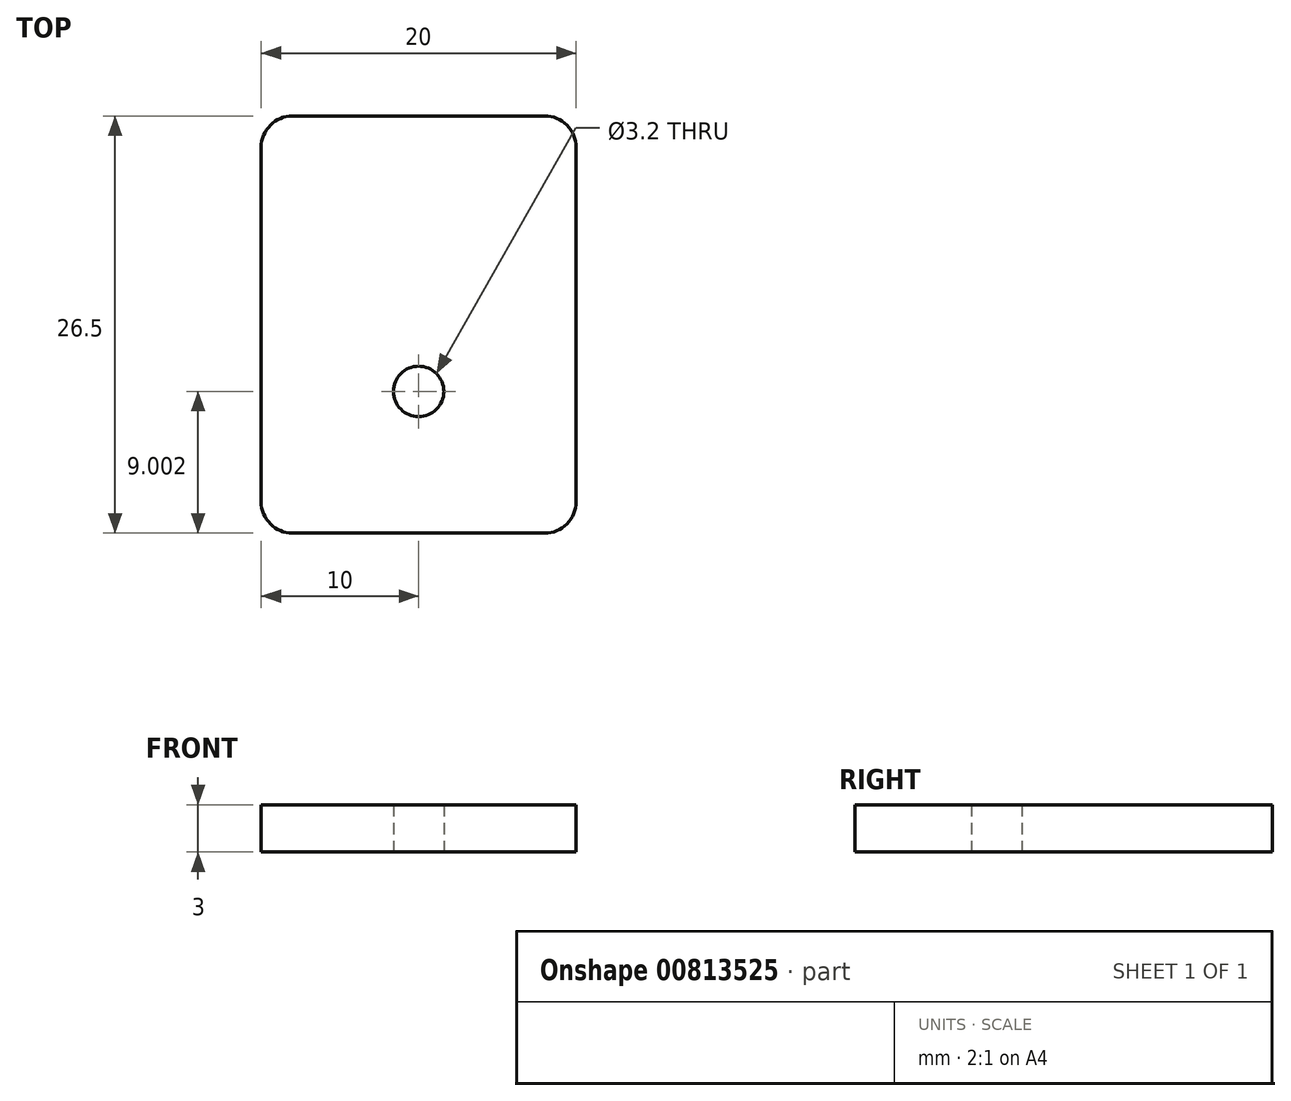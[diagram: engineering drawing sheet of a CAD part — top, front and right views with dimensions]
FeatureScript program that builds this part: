
annotation { "Feature Type Name" : "Feature", "Feature Type Description" : "" }
export const myFeature = defineFeature(function(context is Context, id is Id, definition is map)
    precondition{}
    {
        {
            var Q0;
            Q0=qCreatedBy(makeId("Top.planeOp"),FACE);
            var sketch = newSketch(context, id + "F0", { "sketchPlane" : qUnion([Q0])});
            skArc(sketch, "E0", {"start": v(-8, 13.25) * mm, "mid": v(-9.41, 12.67) * mm, "end": v(-10, 11.25) * mm});
            skLineSegment(sketch, "E1", {"start": v(-8, 13.25) * mm, "end": v(8, 13.25) * mm});
            skArc(sketch, "E2", {"start": v(10, 11.25) * mm, "mid": v(9.41, 12.67) * mm, "end": v(8, 13.25) * mm});
            skCircle(sketch, "E3", {"center": v(0, -4.25) * mm, "radius": 1.6 * mm});
            skLineSegment(sketch, "E4", {"start": v(-10, -11.25) * mm, "end": v(-10, 11.25) * mm});
            skLineSegment(sketch, "E5", {"start": v(10, 11.25) * mm, "end": v(10, -11.25) * mm});
            skArc(sketch, "E6", {"start": v(8, -13.25) * mm, "mid": v(9.41, -12.67) * mm, "end": v(10, -11.25) * mm});
            skArc(sketch, "E7", {"start": v(-10, -11.25) * mm, "mid": v(-9.41, -12.67) * mm, "end": v(-8, -13.25) * mm});
            skLineSegment(sketch, "E8", {"start": v(-8, -13.25) * mm, "end": v(8, -13.25) * mm});
            skSolve(sketch);
        }
        {
            var Q0;
            Q0=makeQuery(id+"F0.imprint","IMPRINT",FACE,{"disambiguationData":[TD([[makeQuery(id+"F0.imprint","IMPRINT",EDGE,{"derivedFrom":sQuery(id+"F0.wireOp",EDGE,"E0")}),1.0]])]});
            extrude(context, id + "F1", {"entities" : qUnion([Q0]), "depth" : 3 * mm, "offsetDistance" : 25 * mm});
        }
    });
